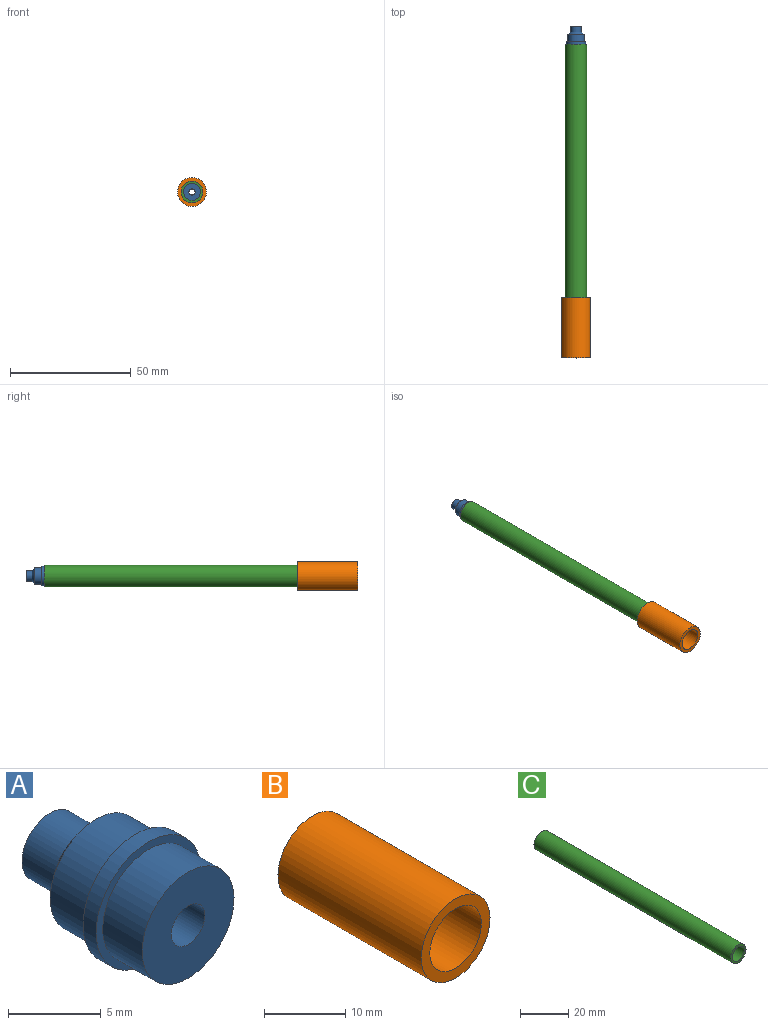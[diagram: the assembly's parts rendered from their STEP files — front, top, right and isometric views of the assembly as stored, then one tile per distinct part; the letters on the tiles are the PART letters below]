
ASSEMBLY  parts=3 mates=4
PART A: 10 faces, bbox 8x10.5x8 mm
  f0: plane 7x7mm, normal (0,-1,0), area 33.4mm2, adj f1,f9
  f1: cylinder r=1.28mm len=10.54mm, axis (0,-1,0), area 84.4mm2, adj f0,f2
  f2: plane 4.22x4.22mm, normal (0,1,0), area 8.9mm2, adj f1,f3
  f3: cylinder r=2.11mm len=4.22mm, axis (0,-1,0), area 33.1mm2, adj f2,f4
  f4: cone r=2.11mm half-angle=53.2deg, axis (0,-1,0), area 30.6mm2, adj f3,f5
  f5: cylinder r=3.5mm len=7mm, axis (0,-1,0), area 66mm2, adj f4,f6
  f6: plane 8x8mm, normal (0,1,0), area 11.8mm2, adj f5,f7
  f7: cylinder r=4mm len=8mm, axis (0,-1,0), area 25.1mm2, adj f6,f8
  f8: plane 8x8mm, normal (0,-1,0), area 11.8mm2, adj f7,f9
  f9: cylinder r=3.5mm len=7mm, axis (0,-1,0), area 66mm2, adj f0,f8
PART B: 4 faces, bbox 12x25x12 mm
  f0: cylinder r=4.5mm len=25mm, axis (0,1,0), area 706.9mm2, adj f2,f3
  f1: cylinder r=6mm len=25mm, axis (0,1,0), area 942.5mm2, adj f2,f3
  f2: plane 12x12mm, normal (0,-1,0), area 49.5mm2, adj f0,f1
  f3: plane 12x12mm, normal (0,1,0), area 49.5mm2, adj f0,f1
PART C: 4 faces, bbox 9x115x9 mm
  f0: cylinder r=3.5mm len=115mm, axis (0,1,0), area 2529mm2, adj f2,f3
  f1: cylinder r=4.5mm len=115mm, axis (0,1,0), area 3251.5mm2, adj f2,f3
  f2: plane 9x9mm, normal (0,-1,0), area 25.1mm2, adj f0,f1
  f3: plane 9x9mm, normal (0,1,0), area 25.1mm2, adj f0,f1
PLACE A rot(axis=(0,1,0),155.4deg) t=(-1.01,59.33,0.62)mm
PLACE B t=(-1.01,-42.67,0.62)mm
PLACE C t=(-1.01,62.33,0.62)mm fixed
MATE cylindrical B.f1 <-> C.f1  axis (0,1,0) through (-1.01,-42.67,0.62)mm
MATE planar B.f1 <-> C.f1  axis (0,-1,0) through (-1.01,-67.67,0.62)mm
MATE cylindrical A.f1 <-> C.f1  axis (0,-1,0) through (-1.01,62.33,0.62)mm
MATE planar A.f1 <-> C.f1  axis (0,-1,0) through (-1.01,62.33,0.62)mm
